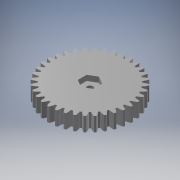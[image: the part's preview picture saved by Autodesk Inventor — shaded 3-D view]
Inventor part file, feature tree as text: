
AUTODESK INVENTOR PART (.ipt)
format: ipt  version: 2017 (Build 210142000, 142)  size: 300,032 bytes
history: native  units: mm (DEFAULTED — no unit token found)
features: sketch x4, extrude x3, plane x3, other x3
ambient origin geometry x8: Origin, YZ Plane, XZ Plane, XY Plane, X Axis, Y Axis, Z Axis, Center Point
bodies: Solid1 (feature_tree)
feature tree (13):
  extrude  "Extrusion1"  Depth=8.0mm TaperAngle=0.0deg
  plane  "Work Plane2"
  plane  "Work Plane8"
  plane  "Work Plane9"
  other  "Spur Gear"
  extrude  "Extrusion2"  Depth=10.0mm TaperAngle=0.0deg
  extrude  "Extrusion3"  Depth=0.872665mm TaperAngle=0.0deg
  sketch  "Sketch1"  dims[d0=47.5mm d1=8.0mm d2=0.0mm]
  sketch  "Sketch2"  dims[d3=45.0mm d4=10.0mm d5=0.0mm]
  other  "Srf1"
  sketch  "Sketch3"  dims[d16=30.0mm d17=0.0mm d34=0.872665mm]
  sketch  "Sketch4"  dims[d39=0.0mm d41=0.0mm d43=30.0mm d46=30.0mm d47=0.0mm d48=0.0mm d49=3.4544mm d50=10.0mm d51=0.0mm d52=10.0838mm d53=3.0mm d54=0.0mm]
  other  "Pitch Diameter"
